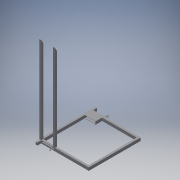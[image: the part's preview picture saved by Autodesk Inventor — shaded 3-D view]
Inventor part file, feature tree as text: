
AUTODESK INVENTOR PART (.ipt)
format: ipt  version: 2018.3 (Build 223284000, 284)  size: 240,640 bytes
history: native  units: mm
features: extrude x9, sketch x9, chamfer x2
ambient origin geometry x8: Origin, YZ Plane, XZ Plane, XY Plane, X Axis, Y Axis, Z Axis, Center Point
bodies: Solid1 (feature_tree)
feature tree (20):
  extrude  "Extrusion1"  Depth=52.5mm
  extrude  "Extrusion2"  Depth=46.0mm
  extrude  "Extrusion3"  Depth=10.0mm TaperAngle=0.0deg
  chamfer  "Chamfer1"  Distance=87.5mm
  chamfer  "Chamfer2"  Distance=2.0mm Angle=60.0deg
  extrude  "Extrusion4"  Depth=10.0mm
  extrude  "Extrusion5"  Depth=1.5mm
  extrude  "Extrusion6"  Depth=10.0mm TaperAngle=0.0deg
  extrude  "Extrusion7"  Depth=1.8mm
  sketch  "Sketch8"  dims[d21=2.85mm d22=10.0mm d23=0.0mm]
  sketch  "Sketch9"  dims[d24=1.0mm d25=1.8mm d26=0.85mm d27=1.25mm d28=1.8mm d29=2.6mm d30=2.6mm d31=1.0mm d32=1.0mm d33=0.5mm d35=4.0mm d36=0.0mm d49=4.0mm d50=0.0mm d51=10.66mm d52=2.54mm d54=0.23mm d55=2.0mm d57=0.23mm d58=6.5mm d59=0.0mm d60=2.0mm d61=30.0deg d62=2.0mm d63=60.0deg d64=0.5mm d65=35.371384mm d74=2.0mm d75=3.0mm d76=0.0mm d77=0.0mm d78=0.0mm d79=0.0mm d81=1.5mm d82=2.0mm d94=0.5mm d95=0.25mm d96=4.0mm d97=0.0mm d98=1.311971mm d99=0.1535mm d100=0.1535mm d101=4.0mm d102=0.0mm d103=0.2mm d104=0.2mm]
  extrude  "Extrusion10"  Depth=0.85mm
  extrude  "Extrusion11"  Depth=1.25mm
  sketch  "Sketch1"  dims[d0=50.0mm d1=52.5mm]
  sketch  "Sketch2"  dims[d2=3.0mm d3=0.0mm d4=46.0mm]
  sketch  "Sketch3"  dims[d5=48.5mm d6=10.0mm d7=0.0mm]
  sketch  "Sketch4"  dims[d8=2.0mm]
  sketch  "Sketch5"  dims[d9=11.7mm d10=87.5mm d11=0.0mm d12=2.0mm d13=2.0mm d14=60.0deg]
  sketch  "Sketch6"  dims[d15=2.0mm d16=2.0mm d17=60.0deg d18=10.0mm]
  sketch  "Sketch7"  dims[d19=1.0mm d20=1.5mm]
